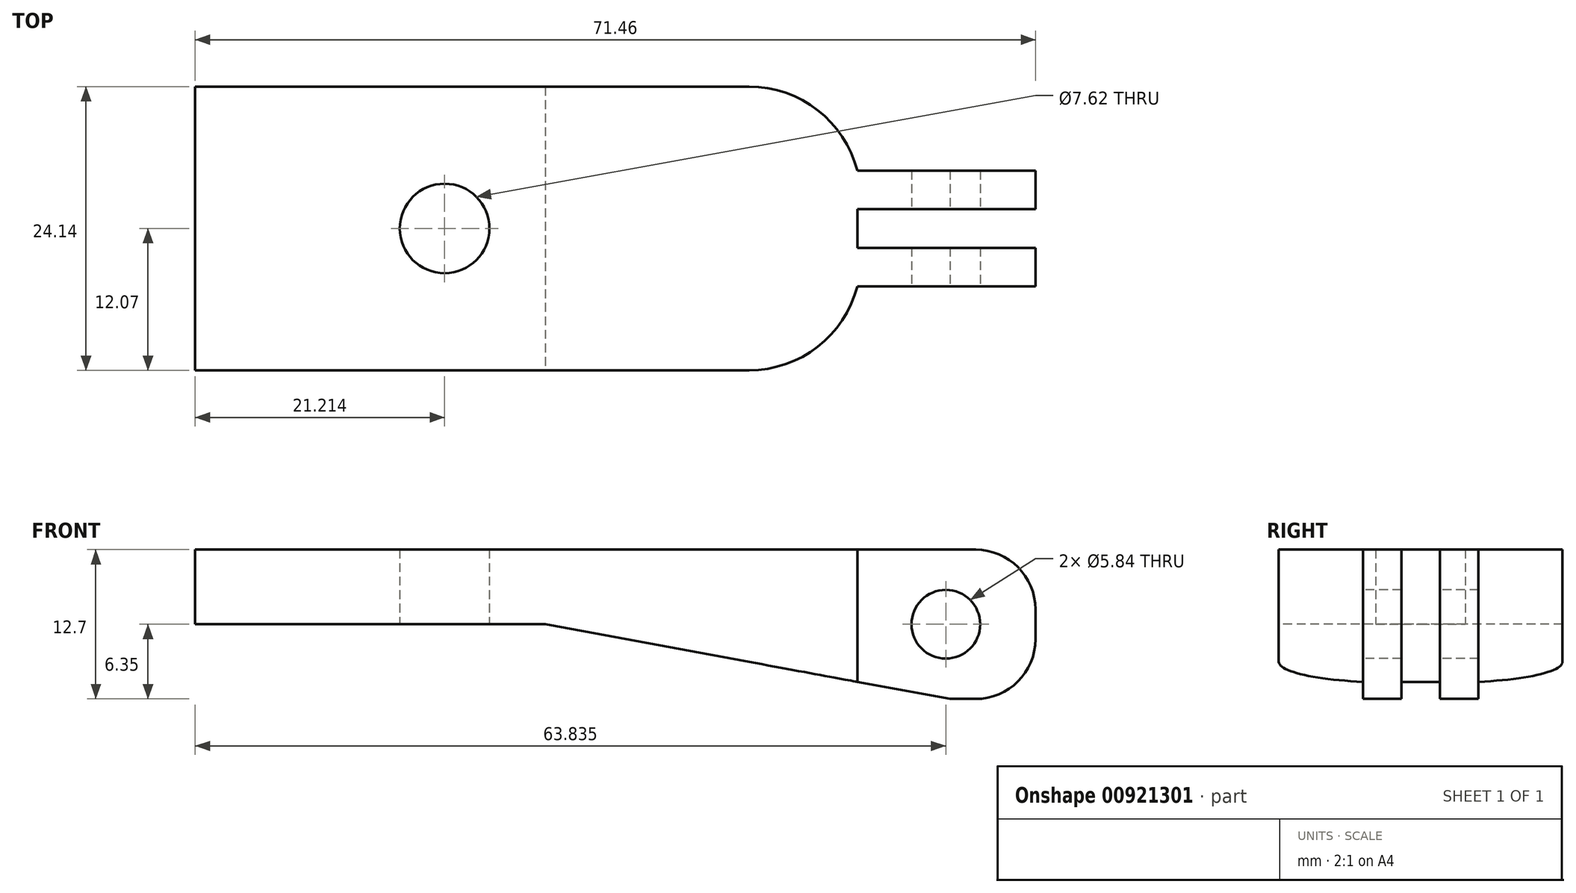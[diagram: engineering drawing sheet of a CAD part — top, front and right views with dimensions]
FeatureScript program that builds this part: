
annotation { "Feature Type Name" : "Feature", "Feature Type Description" : "" }
export const myFeature = defineFeature(function(context is Context, id is Id, definition is map)
    precondition{}
    {
        {
            var Q0;
            Q0=qCreatedBy(makeId("Top.planeOp"),FACE);
            var sketch = newSketch(context, id + "F0", { "sketchPlane" : qUnion([Q0])});
            skLineSegment(sketch, "E0.bottom", {"start": v(-35.73, 12.07) * mm, "end": v(11.38, 12.07) * mm});
            skLineSegment(sketch, "E0.top", {"start": v(-35.73, -12.07) * mm, "end": v(11.38, -12.07) * mm});
            skLineSegment(sketch, "E0.left", {"start": v(-35.73, 12.07) * mm, "end": v(-35.73, -12.07) * mm});
            skLineSegment(sketch, "E0.right", {"start": v(35.73, 4.91) * mm, "end": v(35.73, 1.64) * mm});
            skLineSegment(sketch, "E1", {"start": v(20.57, 1.64) * mm, "end": v(20.57, -1.64) * mm});
            skLineSegment(sketch, "E2.0", {"start": v(20.48, -1.64) * mm, "end": v(35.73, -1.64) * mm});
            skLineSegment(sketch, "E3.0", {"start": v(20.5, 1.64) * mm, "end": v(35.73, 1.64) * mm});
            skLineSegment(sketch, "E4.0", {"start": v(20.57, 4.91) * mm, "end": v(35.73, 4.91) * mm});
            skLineSegment(sketch, "E5.0", {"start": v(20.57, -4.91) * mm, "end": v(35.73, -4.91) * mm});
            skLineSegment(sketch, "E6.trimOffspring", {"start": v(35.73, -1.64) * mm, "end": v(35.73, -4.91) * mm});
            skCircle(sketch, "E7", {"center": v(-14.52, 0) * mm, "radius": 3.81 * mm});
            skArc(sketch, "E8", {"start": v(20.57, 4.91) * mm, "mid": v(17.2, 10.07) * mm, "end": v(11.38, 12.07) * mm});
            skArc(sketch, "E9", {"start": v(11.38, -12.07) * mm, "mid": v(17.2, -10.07) * mm, "end": v(20.57, -4.91) * mm});
            skSolve(sketch);
        }
        {
            var Q0;
            Q0=makeQuery(id+"F0.imprint","IMPRINT",FACE,{"disambiguationData":[TD([[makeQuery(id+"F0.imprint","IMPRINT",EDGE,{"derivedFrom":sQuery(id+"F0.wireOp",EDGE,"E0.bottom")}),-1.0]])]});
            var Q1;
            Q1=makeQuery(id+"F0.imprint","IMPRINT",FACE,{"disambiguationData":[TD([[makeQuery(id+"F0.imprint","IMPRINT",EDGE,{"derivedFrom":sQuery(id+"F0.wireOp",EDGE,"E0.right")}),-1.0]])]});
            var Q2;
            {var subQ2=sQuery(id+"F0.wireOp",EDGE,"E2.0");Q2=makeQuery(id+"F0.imprint","IMPRINT",FACE,{"disambiguationData":[TD([[makeQuery(id+"F0.imprint","IMPRINT",EDGE,{"derivedFrom":subQ2}),-1.0]])]});}
            extrude(context, id + "F1", {"entities" : qUnion([Q0, Q1, Q2]), "depth" : 12.7 * mm, "offsetDistance" : 25.4 * mm});
        }
        {
            var Q0;
            Q0=makeQuery(id+"F1.opExtrude","SWEPT_FACE",FACE,{"disambiguationData":[OSD([sQuery(id+"F0.wireOp",EDGE,"E5.0")])]});
            var sketch = newSketch(context, id + "F2", { "sketchPlane" : qUnion([Q0])});
            skCircle(sketch, "E10", {"center": v(28.1, 6.35) * mm, "radius": 2.92 * mm});
            skPoint(sketch, "E10.centerSnap0", {"position": v(20.49, 6.35) * mm});
            skSolve(sketch);
        }
        {
            var Q0;
            Q0=makeQuery(id+"F1.opExtrude","CAP_EDGE",EDGE,{"disambiguationData":[OSD([sQuery(id+"F0.wireOp",EDGE,"E6.trimOffspring")])],"isStart":false});
            var Q1;
            Q1=makeQuery(id+"F1.opExtrude","CAP_EDGE",EDGE,{"disambiguationData":[OSD([sQuery(id+"F0.wireOp",EDGE,"E0.right")])],"isStart":false});
            var Q2;
            Q2=makeQuery(id+"F1.opExtrude","CAP_EDGE",EDGE,{"disambiguationData":[OSD([sQuery(id+"F0.wireOp",EDGE,"E6.trimOffspring")])],"isStart":true});
            var Q3;
            Q3=makeQuery(id+"F1.opExtrude","CAP_EDGE",EDGE,{"disambiguationData":[OSD([sQuery(id+"F0.wireOp",EDGE,"E0.right")])],"isStart":true});
            fillet(context, id + "F3", {"entities" : qUnion([Q0, Q1, Q2, Q3]), "radius" : 5.08 * mm, "tangentPropagation" : true, "allowEdgeOverflow" : false});
        }
        {
            var Q0;
            Q0=makeQuery(id+"F2.imprint","IMPRINT",FACE,{"disambiguationData":[TD([[makeQuery(id+"F2.imprint","IMPRINT",EDGE,{"derivedFrom":sQuery(id+"F2.wireOp",EDGE,"E10")}),1.0]])]});
            extrude(context, id + "F4", {"entities" : qUnion([Q0]), "operationType" : NewBodyOperationType.REMOVE, "endBound" : BoundingType.THROUGH_ALL, "oppositeDirection" : true, "depth" : 25.4 * mm, "offsetDistance" : 25.4 * mm});
        }
        {
            var Q0;
            Q0=makeQuery(id+"F1.opExtrude","SWEPT_FACE",FACE,{"disambiguationData":[OSD([sQuery(id+"F0.wireOp",EDGE,"E0.top")])]});
            var sketch = newSketch(context, id + "F5", { "sketchPlane" : qUnion([Q0])});
            skLineSegment(sketch, "E11", {"start": v(-35.73, 6.35) * mm, "end": v(-5.97, 6.35) * mm});
            skLineSegment(sketch, "E12", {"start": v(-35.73, 0) * mm, "end": v(-35.73, 0) * mm});
            skLineSegment(sketch, "E13", {"start": v(-35.73, 0) * mm, "end": v(-35.73, 6.35) * mm});
            skLineSegment(sketch, "E14", {"start": v(11.38, 0) * mm, "end": v(-35.73, 0) * mm});
            skLineSegment(sketch, "E15", {"start": v(-5.97, 6.35) * mm, "end": v(28.46, 0) * mm});
            skLineSegment(sketch, "E16", {"start": v(28.46, 0) * mm, "end": v(11.38, 0) * mm});
            skSolve(sketch);
        }
        {
            var Q0;
            Q0=makeQuery(id+"F5.imprint","IMPRINT",FACE,{"disambiguationData":[TD([[makeQuery(id+"F5.imprint","IMPRINT",EDGE,{"derivedFrom":sQuery(id+"F5.wireOp",EDGE,"E11")}),-1.0]])]});
            var Q1;
            {var subQ0=sQuery(id+"F5.wireOp",EDGE,"E16");Q1=makeQuery(id+"F5.imprint","IMPRINT",FACE,{"disambiguationData":[TD([[makeQuery(id+"F5.imprint","IMPRINT",EDGE,{"derivedFrom":subQ0}),-1.0]])]});}
            extrude(context, id + "F6", {"entities" : qUnion([Q0, Q1]), "operationType" : NewBodyOperationType.REMOVE, "endBound" : BoundingType.THROUGH_ALL, "oppositeDirection" : true, "depth" : 25.4 * mm, "offsetDistance" : 25.4 * mm});
        }
    });
